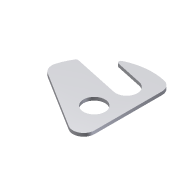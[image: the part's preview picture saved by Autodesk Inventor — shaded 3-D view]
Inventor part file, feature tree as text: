
AUTODESK INVENTOR PART (.ipt)
format: ipt  version: 2012 (Build 160160000, 160)  size: 104,960 bytes
history: native  units: mm
features: extrude x1, sketch x1
ambient origin geometry x8: Origin, YZ Plane, XZ Plane, XY Plane, X Axis, Y Axis, Z Axis, Center Point
feature tree (2):
  extrude  "Extrusion5"  Depth=20.0mm
  sketch  "Sketch1"  dims[d0=108.0mm d4=20.0mm d14=54.0mm d15=54.0mm d16=20.0mm d21=8.0mm d25=54.0mm d28=10.12291mm d30=20.0mm d31=20.0mm d33=21.515487mm d35=13.596647mm d36=2.0mm d37=10.0mm d38=30.0mm d41=20.0mm d42=3.0mm d43=0.0mm]
